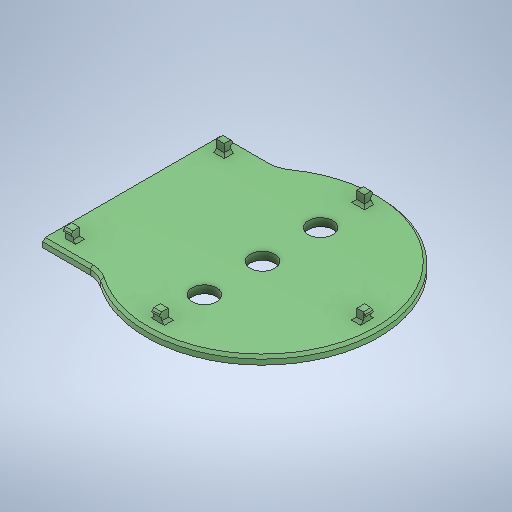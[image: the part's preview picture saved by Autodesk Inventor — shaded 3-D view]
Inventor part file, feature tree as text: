
AUTODESK INVENTOR PART (.ipt)
format: ipt  version: 2025.2 (Build 292293000, 293)  size: 425,984 bytes
history: native  units: mm
features: sketch x6, extrude x5, fillet x2, chamfer x2, sweep x1, pattern_circular x1, mirror x1
ambient origin geometry x8: Origin, YZ Plane, XZ Plane, XY Plane, X Axis, Y Axis, Z Axis, Center Point
bodies: Solid1 (feature_tree)
feature tree (18):
  extrude  "Extrusion1"  Depth=70.0mm
  fillet  "Fillet1"  Radius=50.0mm
  extrude  "Extrusion2"  Depth=10.0mm
  sketch  "Sketch5"  dims[d16=45.0mm d17=9.5mm]
  extrude  "Extrusion3"  Depth=45.0mm
  sweep  "Sweep1"
  pattern_circular  "Circular Pattern1"  [2 undecoded]
  extrude  "Extrusion5"  Depth=3.0mm
  extrude  "Extrusion4"  Depth=0.5mm TaperAngle=0.0deg
  chamfer  "Chamfer1"  Angle=45.0deg  [1 undecoded]
  fillet  "Fillet2"  Radius=1.0mm
  mirror  "Mirror1"
  chamfer  "Chamfer2"  [1 undecoded]
  sketch  "Sketch1"  dims[d0=90.0mm d1=70.0mm d2=50.0mm]
  sketch  "Sketch3"  dims[d3=3.0mm d4=0.0mm d5=10.0mm]
  sketch  "Sketch6"  dims[d18=9.5mm d19=0.0mm]
  sketch  "3D Sketch1"
  sketch  "Sketch7"  dims[d20=4.5mm d21=2.5mm d22=3.0mm d23=4.0mm d24=0.0mm d26=45.0deg d27=1.0mm d28=0.0mm d29=0.0mm d30=20.0mm d31=90.0deg d33=3.0mm d36=45.0deg d37=0.0mm d38=0.0mm d39=4.0mm d40=0.0mm d42=1.0mm d43=1.0mm d44=2.0mm d45=45.0deg d46=0.5mm d47=1.0mm d48=2.0mm d49=45.0deg d51=0.3mm]
note: 4 required parameter values undecoded (feature->parameter linkage not recoverable at this tier; creation-order binding heuristic only, values carry confidence <= 0.55)
